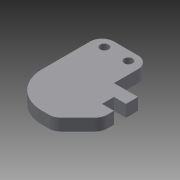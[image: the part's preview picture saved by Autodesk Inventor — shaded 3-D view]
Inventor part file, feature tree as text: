
AUTODESK INVENTOR PART (.ipt)
format: ipt  version: 2015 (Build 190159000, 159)  size: 110,080 bytes
history: native  units: mm
features: extrude x2, sketch x2
ambient origin geometry x8: Origin, YZ Plane, XZ Plane, XY Plane, X Axis, Y Axis, Z Axis, Center Point
bodies: Solid1 (feature_tree)
feature tree (4):
  extrude  "Extrusion1"  Depth=10.0mm
  extrude  "Extrusion2"  Depth=15.0mm
  sketch  "Sketch1"  dims[d0=10.0mm d1=10.0mm]
  sketch  "Sketch2"  dims[d2=20.0mm d3=15.0mm d4=10.0mm d5=5.0mm d6=5.0mm d7=5.0mm d8=135.0deg d9=5.0mm d10=15.0mm d11=5.0mm d12=5.0mm d13=0.0mm d14=6.0mm d15=5.0mm d16=10.0mm d17=3.5mm d18=3.5mm d19=5.0mm d20=0.0mm d21=5.0mm]
